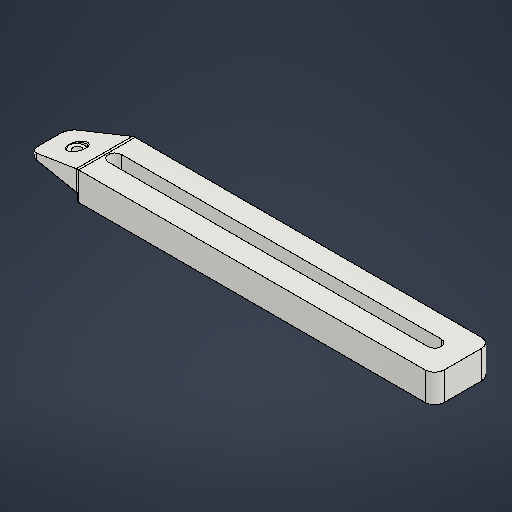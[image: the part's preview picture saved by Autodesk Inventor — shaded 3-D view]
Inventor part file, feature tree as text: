
AUTODESK INVENTOR PART (.ipt)
format: ipt  version: 2025.3 (Build 293356000, 356)  size: 273,920 bytes
history: native  units: mm
features: sketch x4, extrude x3, fillet x2, projected_geometry x2, hole x1, chamfer x1
ambient origin geometry x8: Origin, YZ Plane, XZ Plane, XY Plane, X Axis, Y Axis, Z Axis, Center Point
bodies: Solid1 (feature_tree)
feature tree (13):
  extrude  "Extrusion1"  Depth=30.0mm
  extrude  "Extrusion2"  Depth=170.0mm
  extrude  "Extrusion4"  Depth=20.0mm
  fillet  "Fillet2"  Radius=15.0mm
  fillet  "Fillet1"  [1 undecoded]
  hole  "Hole1"  [1 undecoded]
  chamfer  "Chamfer1"  Distance=5.0mm
  sketch  "Sketch1"  dims[d0=220.0mm d1=30.0mm]
  sketch  "Sketch2"  dims[d2=7.0mm d3=170.0mm]
  sketch  "Sketch3"  dims[d4=15.0mm d6=20.0mm d7=15.0mm d8=0.0mm d12=0.0mm d13=0.0mm]
  projected_geometry  "Projected Loop1"
  sketch  "Sketch5"  dims[d14=0.0mm d15=6.0mm d16=5.0mm d17=4.0mm d18=30.0mm d19=4.5mm d20=6.0mm d21=8.0mm d22=6.0mm d23=90.0deg d24=8.0mm d25=20.594885mm d26=0.5mm d27=2.0mm d28=45.0deg d31=6.0mm d32=170.0mm d33=10.0mm d34=0.0mm d35=3.5mm]
  projected_geometry  "Projected Loop3"
note: 2 required parameter values undecoded (feature->parameter linkage not recoverable at this tier; creation-order binding heuristic only, values carry confidence <= 0.55)
